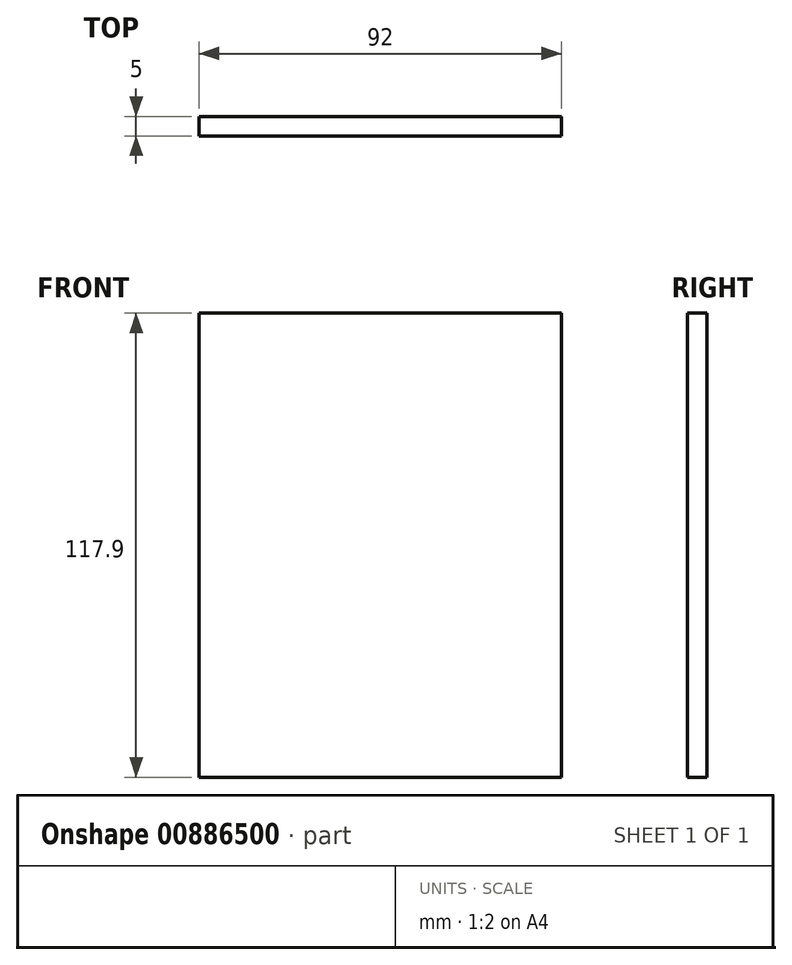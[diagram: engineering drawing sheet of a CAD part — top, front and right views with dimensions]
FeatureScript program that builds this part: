
annotation { "Feature Type Name" : "Feature", "Feature Type Description" : "" }
export const myFeature = defineFeature(function(context is Context, id is Id, definition is map)
    precondition{}
    {
        {
            var Q0;
            Q0=qCreatedBy(makeId("Front.planeOp"),FACE);
            var sketch = newSketch(context, id + "F0", { "sketchPlane" : qUnion([Q0])});
            skLineSegment(sketch, "E0.bottom", {"start": v(-56.03, 28.95) * mm, "end": v(35.97, 28.95) * mm});
            skLineSegment(sketch, "E0.top", {"start": v(-56.03, -88.95) * mm, "end": v(35.97, -88.95) * mm});
            skLineSegment(sketch, "E0.left", {"start": v(-56.03, 28.95) * mm, "end": v(-56.03, -88.95) * mm});
            skLineSegment(sketch, "E0.right", {"start": v(35.97, 28.95) * mm, "end": v(35.97, -88.95) * mm});
            skSolve(sketch);
        }
        {
            var Q0;
            Q0=makeQuery(id+"F0.imprint","IMPRINT",FACE,{"disambiguationData":[TD([[makeQuery(id+"F0.imprint","IMPRINT",EDGE,{"derivedFrom":sQuery(id+"F0.wireOp",EDGE,"E0.bottom")}),-1.0]])]});
            extrude(context, id + "F1", {"entities" : qUnion([Q0]), "depth" : 5 * mm, "offsetDistance" : 25 * mm});
        }
    });
